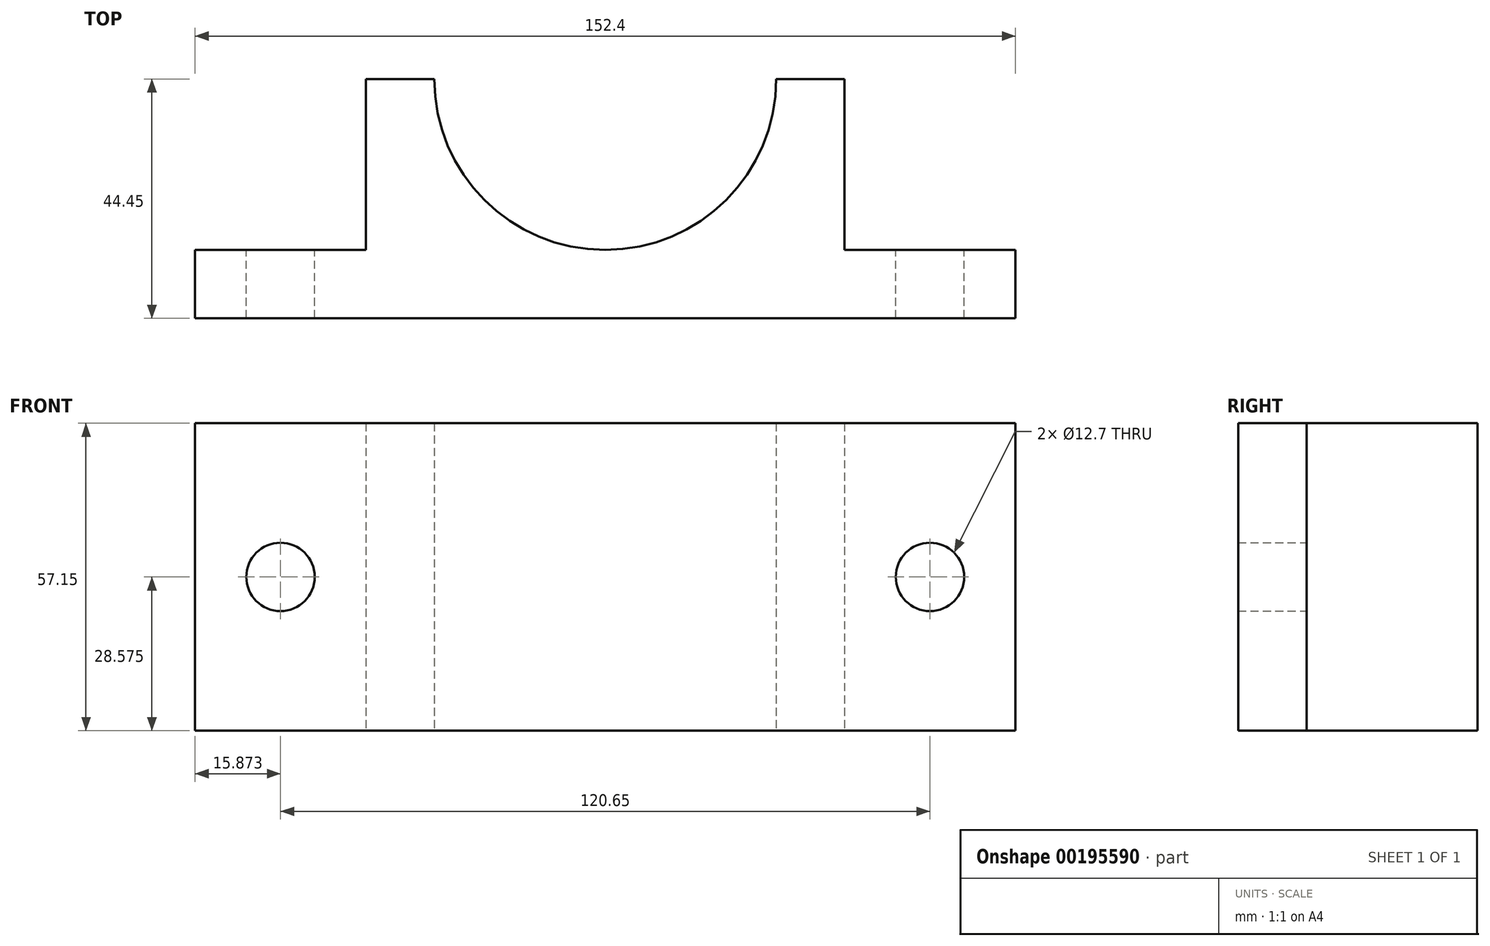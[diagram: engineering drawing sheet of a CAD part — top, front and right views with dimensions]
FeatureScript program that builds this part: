
annotation { "Feature Type Name" : "Feature", "Feature Type Description" : "" }
export const myFeature = defineFeature(function(context is Context, id is Id, definition is map)
    precondition{}
    {
        {
            var Q0;
            Q0=qCreatedBy(makeId("Top.planeOp"),FACE);
            var sketch = newSketch(context, id + "F0", { "sketchPlane" : qUnion([Q0])});
            skLineSegment(sketch, "E0", {"start": v(-72.58, -18.35) * mm, "end": v(79.82, -18.35) * mm});
            skLineSegment(sketch, "E1", {"start": v(79.82, -18.35) * mm, "end": v(79.82, -5.65) * mm});
            skLineSegment(sketch, "E2", {"start": v(-72.58, -18.35) * mm, "end": v(-72.58, -5.65) * mm});
            skLineSegment(sketch, "E3", {"start": v(79.82, -5.65) * mm, "end": v(48.07, -5.65) * mm});
            skLineSegment(sketch, "E4", {"start": v(-72.58, -5.65) * mm, "end": v(-40.83, -5.65) * mm});
            skLineSegment(sketch, "E5", {"start": v(48.07, -5.65) * mm, "end": v(48.07, 26.1) * mm});
            skLineSegment(sketch, "E6", {"start": v(-40.83, -5.65) * mm, "end": v(-40.83, 26.1) * mm});
            skLineSegment(sketch, "E7", {"start": v(48.07, 26.1) * mm, "end": v(35.37, 26.1) * mm});
            skLineSegment(sketch, "E8", {"start": v(-40.83, 26.1) * mm, "end": v(-28.13, 26.1) * mm});
            skArc(sketch, "E9", {"start": v(-28.13, 26.1) * mm, "mid": v(3.62, -5.65) * mm, "end": v(35.37, 26.1) * mm});
            skSolve(sketch);
        }
        {
            var Q0;
            Q0=makeQuery(id+"F0.imprint","IMPRINT",FACE,{"disambiguationData":[TD([[makeQuery(id+"F0.imprint","IMPRINT",EDGE,{"derivedFrom":sQuery(id+"F0.wireOp",EDGE,"E0")}),1.0]])]});
            extrude(context, id + "F1", {"entities" : qUnion([Q0]), "depth" : 57.15 * mm});
        }
        {
            var Q0;
            Q0=makeQuery(id+"F1.opExtrude","SWEPT_FACE",FACE,{"disambiguationData":[OSD([sQuery(id+"F0.wireOp",EDGE,"E3")])]});
            var sketch = newSketch(context, id + "F2", { "sketchPlane" : qUnion([Q0])});
            skLineSegment(sketch, "E10", {"start": v(-79.82, 57.15) * mm, "end": v(-79.82, 28.58) * mm});
            skLineSegment(sketch, "E11", {"start": v(-48.07, 57.15) * mm, "end": v(-63.94, 57.15) * mm});
            skCircle(sketch, "E12", {"center": v(-63.94, 28.58) * mm, "radius": 6.35 * mm});
            skSolve(sketch);
        }
        {
            var Q0;
            Q0=makeQuery(id+"F1.opExtrude","SWEPT_FACE",FACE,{"disambiguationData":[OSD([sQuery(id+"F0.wireOp",EDGE,"E4")])]});
            var sketch = newSketch(context, id + "F3", { "sketchPlane" : qUnion([Q0])});
            skCircle(sketch, "E13", {"center": v(56.7, 28.58) * mm, "radius": 6.35 * mm});
            skSolve(sketch);
        }
        {
            var Q0;
            Q0=makeQuery(id+"F3.imprint","IMPRINT",FACE,{"disambiguationData":[TD([[makeQuery(id+"F3.imprint","IMPRINT",EDGE,{"derivedFrom":sQuery(id+"F3.wireOp",EDGE,"E13")}),1.0]])]});
            extrude(context, id + "F4", {"entities" : qUnion([Q0]), "operationType" : NewBodyOperationType.REMOVE, "endBound" : BoundingType.THROUGH_ALL, "oppositeDirection" : true, "depth" : 25.4 * mm});
        }
        {
            var Q0;
            Q0=makeQuery(id+"F2.imprint","IMPRINT",FACE,{"disambiguationData":[TD([[makeQuery(id+"F2.imprint","IMPRINT",EDGE,{"derivedFrom":sQuery(id+"F2.wireOp",EDGE,"E12")}),1.0]])]});
            extrude(context, id + "F5", {"entities" : qUnion([Q0]), "operationType" : NewBodyOperationType.REMOVE, "endBound" : BoundingType.THROUGH_ALL, "oppositeDirection" : true, "depth" : 25.4 * mm});
        }
    });
